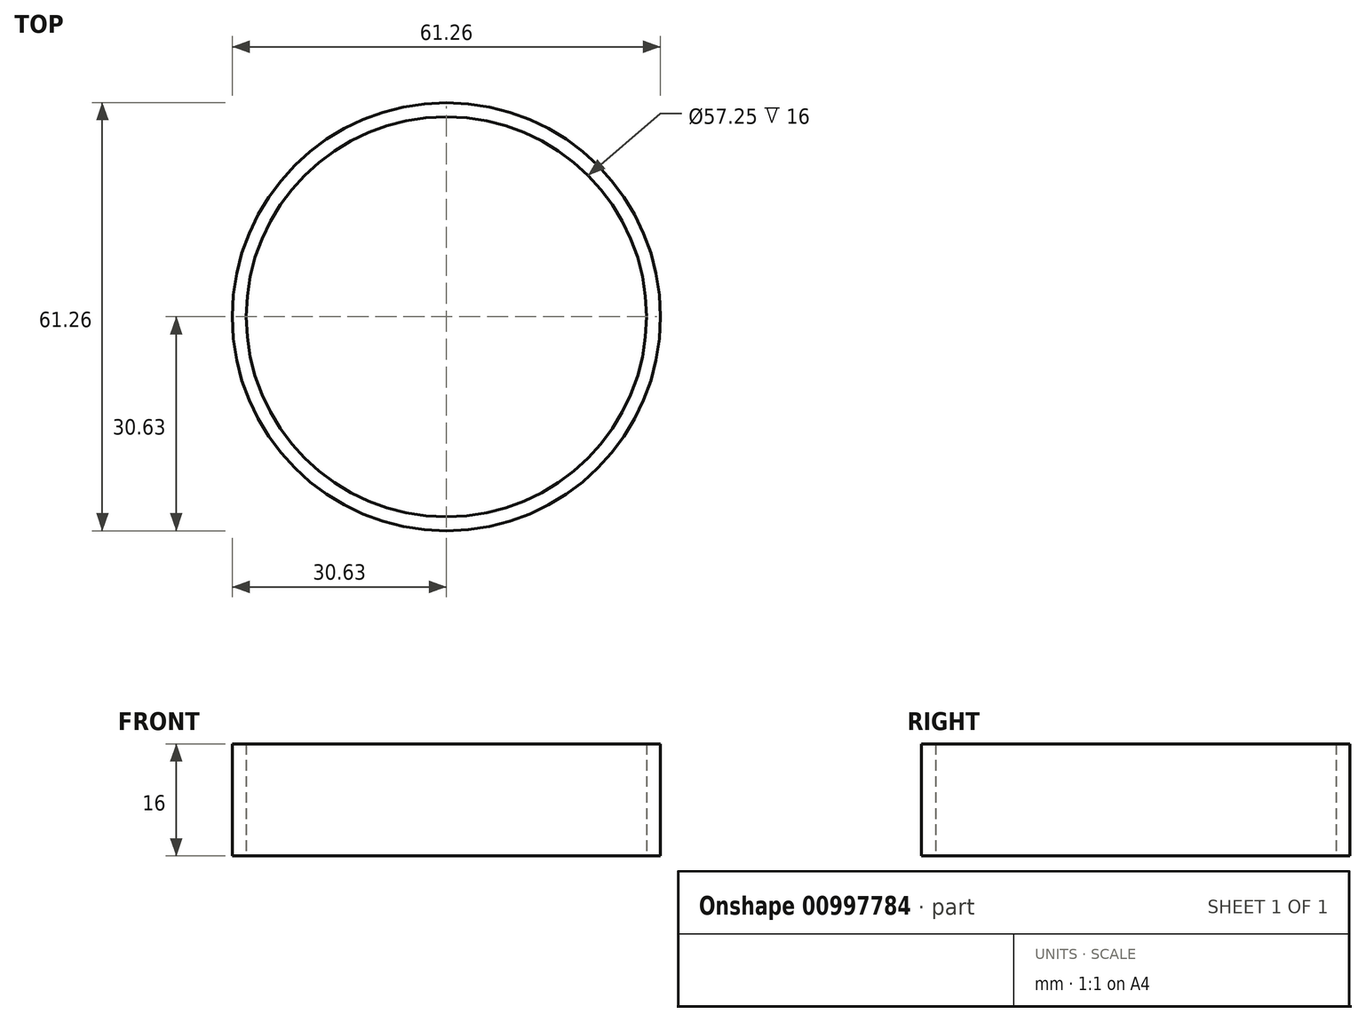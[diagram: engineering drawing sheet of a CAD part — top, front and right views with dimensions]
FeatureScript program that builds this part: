
annotation { "Feature Type Name" : "Feature", "Feature Type Description" : "" }
export const myFeature = defineFeature(function(context is Context, id is Id, definition is map)
    precondition{}
    {
        {
            var Q0;
            Q0=qCreatedBy(makeId("Top.planeOp"),FACE);
            var sketch = newSketch(context, id + "F0", { "sketchPlane" : qUnion([Q0])});
            skCircle(sketch, "E0", {"center": v(0, 0) * mm, "radius": 28.62 * mm});
            skCircle(sketch, "E1", {"center": v(0, 0) * mm, "radius": 30.62 * mm});
            skSolve(sketch);
        }
        {
            var Q0;
            Q0 = qSketchRegion(id + "F0", true);
            extrude(context, id + "F1", {"entities" : qUnion([Q0]), "depth" : 16 * mm, "offsetDistance" : 25.4 * mm});
        }
    });
